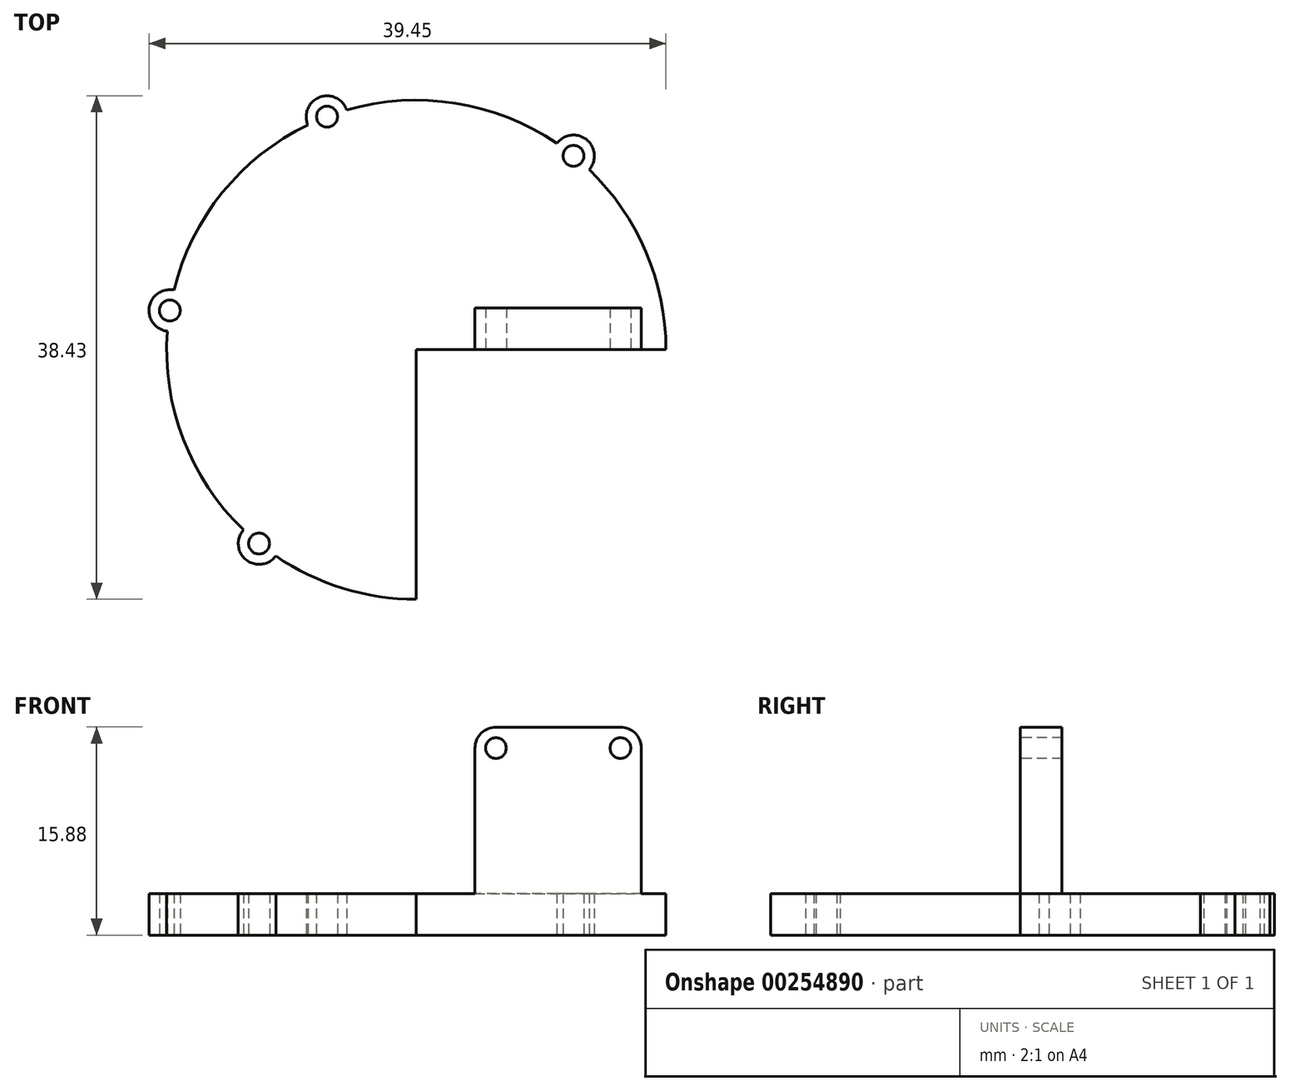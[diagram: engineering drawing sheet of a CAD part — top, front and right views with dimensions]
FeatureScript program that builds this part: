
annotation { "Feature Type Name" : "Feature", "Feature Type Description" : "" }
export const myFeature = defineFeature(function(context is Context, id is Id, definition is map)
    precondition{}
    {
        {
            var Q0;
            Q0=qCreatedBy(makeId("Top.planeOp"),FACE);
            var sketch = newSketch(context, id + "F0", { "sketchPlane" : qUnion([Q0])});
            skArc(sketch, "E0", {"start": v(19.05, 0) * mm, "mid": v(-13.47, 13.47) * mm, "end": v(0, -19.05) * mm});
            skLineSegment(sketch, "E1", {"start": v(0, 0) * mm, "end": v(0, -19.05) * mm});
            skLineSegment(sketch, "E2", {"start": v(0, -19.05) * mm, "end": v(0, 0) * mm});
            skLineSegment(sketch, "E3", {"start": v(0, 0) * mm, "end": v(19.05, 0) * mm});
            skArc(sketch, "E4", {"start": v(-5.31, 18.3) * mm, "mid": v(-7.38, 19.27) * mm, "end": v(-8.27, 17.16) * mm});
            skCircle(sketch, "E5", {"center": v(-6.82, 17.79) * mm, "radius": 0.8 * mm});
            skLineSegment(sketch, "E6", {"start": v(0, -41.6) * mm, "end": v(0, 43.36) * mm, "construction": true});
            skCircle(sketch, "E7.1.0", {"center": v(-18.81, 3) * mm, "radius": 0.8 * mm});
            skArc(sketch, "E7.1.1", {"start": v(-18.5, 4.55) * mm, "mid": v(-20.38, 3.24) * mm, "end": v(-19, 1.42) * mm});
            skCircle(sketch, "E7.2.0", {"center": v(-12, -14.8) * mm, "radius": 0.8 * mm});
            skArc(sketch, "E7.2.1", {"start": v(-13.19, -13.75) * mm, "mid": v(-13, -16.03) * mm, "end": v(-10.72, -15.74) * mm});
            skCircle(sketch, "E7.5.0", {"center": v(12, 14.8) * mm, "radius": 0.8 * mm});
            skArc(sketch, "E7.5.1", {"start": v(13.19, 13.75) * mm, "mid": v(13, 16.03) * mm, "end": v(10.72, 15.74) * mm});
            skSolve(sketch);
        }
        {
            var Q0;
            Q0 = qSketchRegion(id + "F0", true);
            extrude(context, id + "F1", {"entities" : qUnion([Q0]), "depth" : 3.17 * mm});
        }
        {
            var Q0;
            Q0=makeQuery(id+"F1.opExtrude","CAP_FACE",FACE,{"disambiguationData":[OSD([sQuery(id+"F0.wireOp",EDGE,"E0"),sQuery(id+"F0.wireOp",EDGE,"E2"),sQuery(id+"F0.wireOp",EDGE,"E3"),sQuery(id+"F0.wireOp",EDGE,"E5"),sQuery(id+"F0.wireOp",EDGE,"E4"),sQuery(id+"F0.wireOp",EDGE,"E7.1.0"),sQuery(id+"F0.wireOp",EDGE,"E7.1.1"),sQuery(id+"F0.wireOp",EDGE,"E7.2.0"),sQuery(id+"F0.wireOp",EDGE,"E7.2.1"),sQuery(id+"F0.wireOp",EDGE,"E7.5.0"),sQuery(id+"F0.wireOp",EDGE,"E7.5.1")])],"isStart":false});
            var sketch = newSketch(context, id + "F2", { "sketchPlane" : qUnion([Q0])});
            skLineSegment(sketch, "E8", {"start": v(4.48, 0) * mm, "end": v(4.48, 3.18) * mm});
            skLineSegment(sketch, "E9", {"start": v(4.48, 3.18) * mm, "end": v(17.18, 3.18) * mm});
            skLineSegment(sketch, "E10", {"start": v(17.18, 3.18) * mm, "end": v(17.18, 0) * mm});
            skLineSegment(sketch, "E11", {"start": v(4.48, 0) * mm, "end": v(17.18, 0) * mm});
            skSolve(sketch);
        }
        {
            var Q0;
            Q0 = qSketchRegion(id + "F2", true);
            extrude(context, id + "F3", {"entities" : qUnion([Q0]), "operationType" : NewBodyOperationType.ADD, "depth" : 12.7 * mm});
        }
        {
            var Q0;
            Q0=makeQuery(id+"F3.opExtrude","CAP_EDGE",EDGE,{"disambiguationData":[OSD([sQuery(id+"F2.wireOp",EDGE,"E10")])],"isStart":false});
            var Q1;
            Q1=makeQuery(id+"F3.opExtrude","CAP_EDGE",EDGE,{"disambiguationData":[OSD([sQuery(id+"F2.wireOp",EDGE,"E8")])],"isStart":false});
            fillet(context, id + "F4", {"entities" : qUnion([Q0, Q1]), "radius" : 1.6 * mm, "tangentPropagation" : true, "allowEdgeOverflow" : false});
        }
        {
            var Q0;
            Q0=makeQuery(id+"F3.boolean.opBoolean","MERGE",FACE,{"derivedFrom":[makeQuery(id+"F1.opExtrude","SWEPT_FACE",FACE,{"disambiguationData":[OSD([sQuery(id+"F0.wireOp",EDGE,"E3")])]}),makeQuery(id+"F3.opExtrude","SWEPT_FACE",FACE,{"disambiguationData":[OSD([sQuery(id+"F2.wireOp",EDGE,"E11")])]})]});
            var sketch = newSketch(context, id + "F5", { "sketchPlane" : qUnion([Q0])});
            skCircle(sketch, "E12", {"center": v(15.58, 14.27) * mm, "radius": 0.79 * mm});
            skCircle(sketch, "E13", {"center": v(6.08, 14.27) * mm, "radius": 0.79 * mm});
            skSolve(sketch);
        }
        {
            var Q0;
            Q0 = qSketchRegion(id + "F5", true);
            extrude(context, id + "F6", {"entities" : qUnion([Q0]), "operationType" : NewBodyOperationType.REMOVE, "endBound" : BoundingType.THROUGH_ALL, "oppositeDirection" : true, "depth" : 25.4 * mm});
        }
    });
